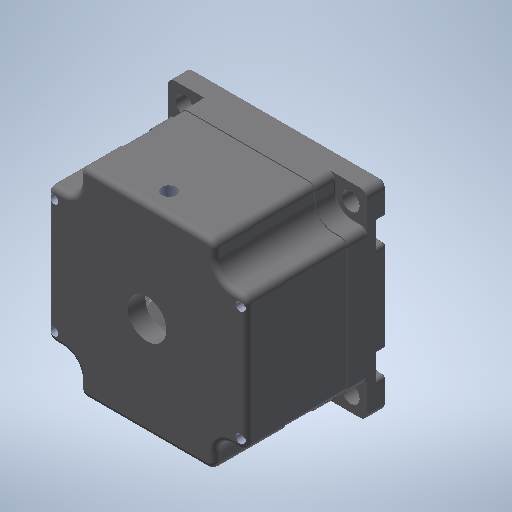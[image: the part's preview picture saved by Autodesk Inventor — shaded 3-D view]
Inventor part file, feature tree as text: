
AUTODESK INVENTOR PART (.ipt)
format: ipt  version: 2025.1 (Build 291241000, 241)  size: 596,992 bytes
history: native  units: mm
features: other x1, imported_body x1, extrude x1, sketch x1
ambient origin geometry x8: Origin, YZ Plane, XZ Plane, XY Plane, X Axis, Y Axis, Z Axis, Center Point
bodies: Body1 (feature_tree)
feature tree (4):
  other  "NEMA 23 - 41mm"
  imported_body  "Base1"
  extrude  "Extrusion1"  Depth=2.0mm
  sketch  "Sketch1"  dims[d3=0.0mm d4=0.0mm d6=2.0mm d7=5.85mm d8=2.0mm]
